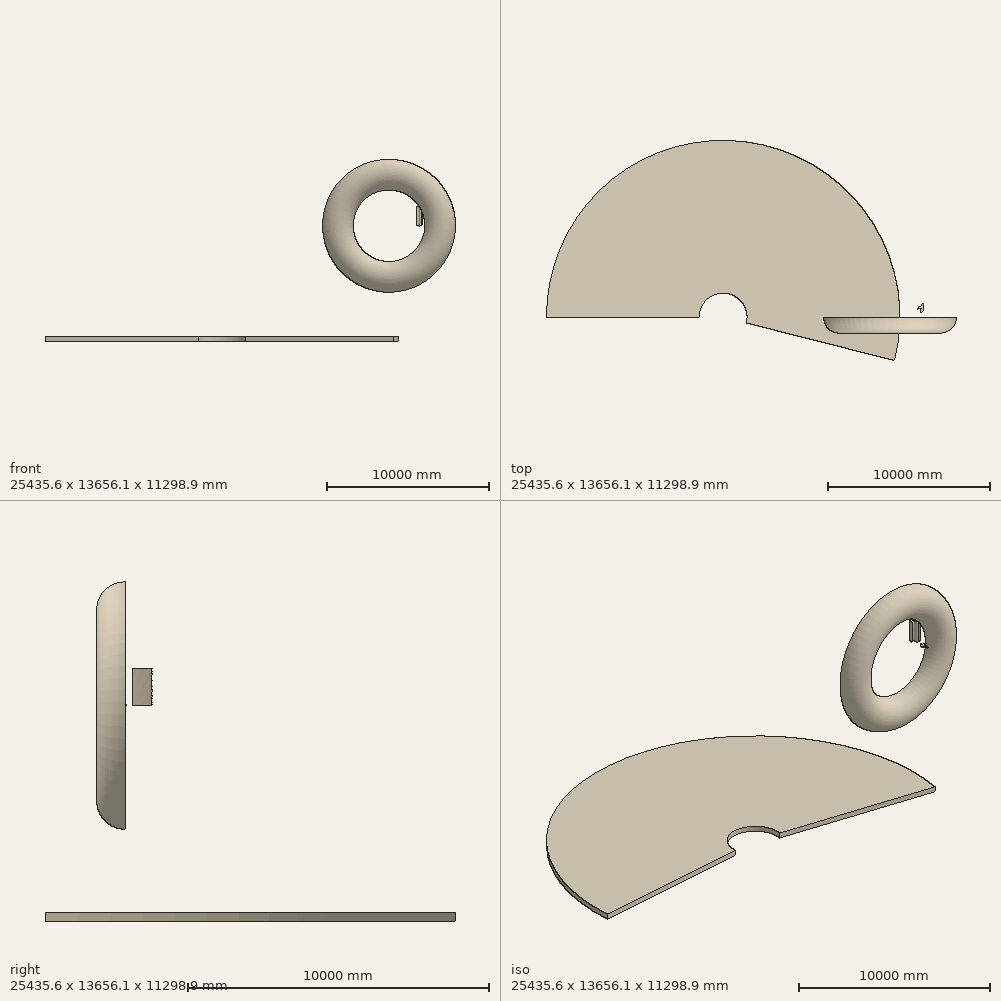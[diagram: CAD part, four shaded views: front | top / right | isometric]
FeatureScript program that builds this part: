
annotation { "Feature Type Name" : "Feature", "Feature Type Description" : "" }
export const myFeature = defineFeature(function(context is Context, id is Id, definition is map)
    precondition{}
    {
        {
            var Q0;
            Q0=qCreatedBy(makeId("Top.planeOp"),FACE);
            var sketch = newSketch(context, id + "F0", { "sketchPlane" : qUnion([Q0])});
            skLineSegment(sketch, "E0.bottom", {"start": v(92.01, -36.07) * mm, "end": v(2632.65, -36.07) * mm});
            skLineSegment(sketch, "E0.top", {"start": v(92.01, 26.16) * mm, "end": v(2632.65, 26.16) * mm});
            skLineSegment(sketch, "E0.left", {"start": v(92.01, -36.07) * mm, "end": v(92.01, 26.16) * mm});
            skLineSegment(sketch, "E0.right", {"start": v(2632.65, -36.07) * mm, "end": v(2632.65, 26.16) * mm});
            skCircle(sketch, "E1", {"center": v(1260.53, -36.07) * mm, "radius": 952.82 * mm});
            skLineSegment(sketch, "E2", {"start": v(3070.5, 365.53) * mm, "end": v(3158.96, -409.32) * mm});
            skLineSegment(sketch, "E3", {"start": v(-1908.37, -1224.54) * mm, "end": v(-1908.37, 739.22) * mm, "construction": true});
            skSolve(sketch);
        }
        {
            var Q0;
            Q0=sQuery(id+"F0.wireOp",EDGE,"E0.top");
            var Q1;
            Q1=sQuery(id+"F0.wireOp",EDGE,"E0.bottom");
            var Q2;
            Q2=sQuery(id+"F0.wireOp",EDGE,"E2");
            revolve(context, id + "F1", {"bodyType" : ToolBodyType.SURFACE, "surfaceEntities" : qUnion([Q0, Q1]), "axis" : qUnion([Q2]), "revolveType" : RevolveType.FULL});
        }
        {
            var Q0;
            {var subQ0=sQuery(id+"F0.wireOp",EDGE,"E1");var subQ1=sQuery(id+"F0.wireOp",EDGE,"E0.bottom");var subQ2=makeQuery(id+"F0.imprint","INTERSECT",VERTEX,{"disambiguationData":[OD(0.0)],"derivedFrom":[subQ1,subQ0]});Q0=makeQuery(id+"F0.imprint","IMPRINT",FACE,{"disambiguationData":[TD([[makeQuery(id+"F0.imprint","IMPRINT",EDGE,{"disambiguationData":[TD([[subQ2,-1.0]])],"derivedFrom":subQ1}),-1.0]])]});}
            var Q1;
            Q1=sQuery(id+"F0.wireOp",EDGE,"E3");
            revolve(context, id + "F12", {"entities" : qUnion([Q0]), "axis" : qUnion([Q1]), "revolveType" : RevolveType.FULL});
        }
        {
            var Q0;
            Q0=qCreatedBy(makeId("Front.planeOp"),FACE);
            var sketch = newSketch(context, id + "F13", { "sketchPlane" : qUnion([Q0])});
            skLineSegment(sketch, "E4.bottom", {"start": v(-13740.44, -6881.52) * mm, "end": v(-23222.2, -6881.52) * mm});
            skLineSegment(sketch, "E4.top", {"start": v(-13740.44, -7177.15) * mm, "end": v(-23222.2, -7177.15) * mm});
            skLineSegment(sketch, "E4.left", {"start": v(-13740.44, -6881.52) * mm, "end": v(-13740.44, -7177.15) * mm});
            skLineSegment(sketch, "E4.right", {"start": v(-23222.2, -6881.52) * mm, "end": v(-23222.2, -7177.15) * mm});
            skLineSegment(sketch, "E5", {"start": v(-12259.04, -6137.5) * mm, "end": v(-12259.04, -8157.46) * mm, "construction": true});
            skSolve(sketch);
        }
        {
            var Q0;
            Q0=makeQuery(id+"F13.imprint","IMPRINT",FACE,{"disambiguationData":[TD([[makeQuery(id+"F13.imprint","IMPRINT",EDGE,{"derivedFrom":sQuery(id+"F13.wireOp",EDGE,"E4.bottom")}),1.0]])]});
            var Q1;
            Q1=sQuery(id+"F13.wireOp",EDGE,"E5");
            revolve(context, id + "F14", {"entities" : qUnion([Q0]), "axis" : qUnion([Q1]), "revolveType" : RevolveType.ONE_DIRECTION, "angle" : 194.22 * degree});
        }
        {
            var Q0;
            Q0=qCreatedBy(makeId("Front.planeOp"),FACE);
            var sketch = newSketch(context, id + "F15", { "sketchPlane" : qUnion([Q0])});
            skCircle(sketch, "E6", {"center": v(0, 0) * mm, "radius": 35.02 * mm});
            skSolve(sketch);
        }
        {
            var Q0;
            Q0 = qSketchRegion(id + "F15", true);
            extrude(context, id + "F16", {"entities" : qUnion([Q0]), "depth" : 23.8 * mm});
        }
        {
            var Q0;
            Q0=makeQuery(id+"F16.opExtrude","CAP_EDGE",EDGE,{"disambiguationData":[OSD([sQuery(id+"F15.wireOp",EDGE,"E6")])],"isStart":false});
            var Q1;
            Q1=makeQuery(id+"F16.opExtrude","CAP_EDGE",EDGE,{"disambiguationData":[OSD([sQuery(id+"F15.wireOp",EDGE,"E6")])],"isStart":true});
            fillet(context, id + "F17", {"entities" : qUnion([Q0, Q1]), "radius" : 3.17 * mm, "tangentPropagation" : true, "allowEdgeOverflow" : false});
        }
        {
            var Q0;
            Q0=qCreatedBy(makeId("Right.planeOp"),FACE);
            var sketch = newSketch(context, id + "F2", { "sketchPlane" : qUnion([Q0])});
            skLineSegment(sketch, "E7", {"start": v(-3.18, -35.02) * mm, "end": v(-20.64, -35.02) * mm});
            skLineSegment(sketch, "E8", {"start": v(-20.64, 35.02) * mm, "end": v(-3.18, 35.02) * mm});
            skCircle(sketch, "E9", {"center": v(-12.03, 2.87) * mm, "radius": 4.97 * mm});
            skLineSegment(sketch, "E10", {"start": v(-70.86, 0) * mm, "end": v(33.05, 0) * mm, "construction": true});
            skSolve(sketch);
        }
        {
            var Q0;
            Q0 = qSketchRegion(id + "F2", true);
            extrude(context, id + "F3", {"entities" : qUnion([Q0]), "operationType" : NewBodyOperationType.REMOVE, "endBound" : BoundingType.UP_TO_NEXT, "oppositeDirection" : true, "depth" : 25.4 * mm});
        }
        {
            var Q0;
            Q0=makeQuery(id+"F16.opExtrude","SWEPT_BODY",BODY,{"disambiguationData":[OSD([sQuery(id+"F15.wireOp",EDGE,"E6")])]});
            var Q1;
            Q1=sQuery(id+"F2.wireOp",EDGE,"E10");
            circularPattern(context, id + "F4", {"entities" : qUnion([Q0]), "axis" : qUnion([Q1]), "angle" : 360 * degree, "instanceCount" : 4, "equalSpace" : true});
        }
        {
            var Q0;
            Q0=qCreatedBy(makeId("Top.planeOp"),FACE);
            var sketch = newSketch(context, id + "F18", { "sketchPlane" : qUnion([Q0])});
            skFitSpline(sketch, "E11", {"points": [v(48.55, -173.31) * mm, v(174.03, -207.84) * mm, v(-172.04, -133.26) * mm, v(-39.91, -410.74) * mm], "startDerivative": vector(973.41, -839.18) * mm, "endDerivative": vector(668.36, 461.78) * mm});
            skFitSpline(sketch, "E12", {"points": [v(-260.6, 355.06) * mm, v(21.41, 497.79) * mm, v(-15.8, 374.19) * mm, v(85.32, 312.25) * mm], "startDerivative": vector(565.05, 1513.97) * mm, "endDerivative": vector(221.65, 1520) * mm});
            skFitSpline(sketch, "E13", {"points": [v(173.83, 382.94) * mm, v(146.98, 851.05) * mm, v(-80.23, 756.18) * mm], "startDerivative": vector(59.43, -2905.2) * mm, "endDerivative": vector(-550.41, 2215.66) * mm});
            skLineSegment(sketch, "E14", {"start": v(-39.91, -410.74) * mm, "end": v(-24.84, -592.9) * mm});
            skLineSegment(sketch, "E15", {"start": v(-24.84, -592.9) * mm, "end": v(48.55, -173.31) * mm});
            skLineSegment(sketch, "E16", {"start": v(85.32, 312.25) * mm, "end": v(173.83, 382.94) * mm});
            skLineSegment(sketch, "E17", {"start": v(-260.6, 355.06) * mm, "end": v(-80.23, 756.18) * mm});
            skSolve(sketch);
        }
        {
            var Q0;
            Q0=makeQuery(id+"F18.imprint","IMPRINT",FACE,{"disambiguationData":[TD([[makeQuery(id+"F18.imprint","IMPRINT",EDGE,{"derivedFrom":sQuery(id+"F18.wireOp",EDGE,"E11")}),1.0]])]});
            extrude(context, id + "F5", {"entities" : qUnion([Q0]), "depth" : ((12 * 3)) * mm});
        }
        {
            var Q0;
            {var subQ4=sQuery(id+"F18.wireOp",EDGE,"E13");Q0=makeQuery(id+"F18.imprint","IMPRINT",FACE,{"disambiguationData":[TD([[makeQuery(id+"F18.imprint","IMPRINT",EDGE,{"derivedFrom":subQ4}),1.0]])]});}
            extrude(context, id + "F6", {"entities" : qUnion([Q0]), "depth" : 1219.2 * mm});
        }
        {
            var Q0;
            Q0=qCreatedBy(makeId("Top.planeOp"),FACE);
            var sketch = newSketch(context, id + "F19", { "sketchPlane" : qUnion([Q0])});
            skLineSegment(sketch, "E18", {"start": v(0, 76) * mm, "end": v(48.41, 0) * mm});
            skLineSegment(sketch, "E19", {"start": v(48.41, 0) * mm, "end": v(-48.41, 0) * mm});
            skLineSegment(sketch, "E20", {"start": v(-48.41, 0) * mm, "end": v(0, 76) * mm});
            skLineSegment(sketch, "E21", {"start": v(-69.43, -15.77) * mm, "end": v(63.9, -15.77) * mm, "construction": true});
            skLineSegment(sketch, "E22.MirrorCS", {"start": v(0, -107.54) * mm, "end": v(48.41, -31.54) * mm});
            skLineSegment(sketch, "E23.MirrorCS", {"start": v(48.41, -31.54) * mm, "end": v(-48.41, -31.54) * mm});
            skLineSegment(sketch, "E24.MirrorCS", {"start": v(-48.41, -31.54) * mm, "end": v(0, -107.54) * mm});
            skSolve(sketch);
        }
        {
            var Q0;
            Q0 = qSketchRegion(id + "F19", true);
            var Q1;
            Q1=sQuery(id+"F19.wireOp",EDGE,"E20");
            var Q2;
            Q2=sQuery(id+"F19.wireOp",EDGE,"E18");
            var Q3;
            Q3=sQuery(id+"F19.wireOp",EDGE,"E19");
            var Q4;
            Q4=sQuery(id+"F19.wireOp",EDGE,"E23.MirrorCS");
            var Q5;
            Q5=sQuery(id+"F19.wireOp",EDGE,"E22.MirrorCS");
            var Q6;
            Q6=sQuery(id+"F19.wireOp",EDGE,"E24.MirrorCS");
            extrude(context, id + "F7", {"entities" : qUnion([Q0]), "bodyType" : ToolBodyType.SURFACE, "surfaceEntities" : qUnion([Q1, Q2, Q3, Q4, Q5, Q6]), "endBound" : BoundingType.SYMMETRIC, "depth" : 152.4 * mm});
        }
        {
            var Q0;
            Q0=qCreatedBy(makeId("Top.planeOp"),FACE);
            var sketch = newSketch(context, id + "F8", { "sketchPlane" : qUnion([Q0])});
            skCircle(sketch, "E25.cCircle", {"center": v(823.84, 0) * mm, "radius": 155.72 * mm, "construction": true});
            skLineSegment(sketch, "E25.0", {"start": v(989.63, -69.6) * mm, "end": v(846.46, -178.38) * mm});
            skLineSegment(sketch, "E25.1", {"start": v(846.46, -178.38) * mm, "end": v(680.66, -108.78) * mm});
            skLineSegment(sketch, "E25.2", {"start": v(680.66, -108.78) * mm, "end": v(658.05, 69.6) * mm});
            skLineSegment(sketch, "E25.3", {"start": v(658.05, 69.6) * mm, "end": v(801.22, 178.38) * mm});
            skLineSegment(sketch, "E25.4", {"start": v(801.22, 178.38) * mm, "end": v(967.02, 108.78) * mm});
            skLineSegment(sketch, "E25.5", {"start": v(967.02, 108.78) * mm, "end": v(989.63, -69.6) * mm});
            skPoint(sketch, "E25.0.midPoint", {"position": v(918.04, -124) * mm});
            skCircle(sketch, "E26.cCircle", {"center": v(814.87, 558.57) * mm, "radius": 188.4 * mm, "construction": true});
            skLineSegment(sketch, "E26.0", {"start": v(1003.28, 695.46) * mm, "end": v(1003.28, 421.69) * mm});
            skLineSegment(sketch, "E26.1", {"start": v(1003.28, 421.69) * mm, "end": v(742.9, 337.09) * mm});
            skLineSegment(sketch, "E26.2", {"start": v(742.9, 337.09) * mm, "end": v(581.98, 558.57) * mm});
            skLineSegment(sketch, "E26.3", {"start": v(581.98, 558.57) * mm, "end": v(742.9, 780.06) * mm});
            skLineSegment(sketch, "E26.4", {"start": v(742.9, 780.06) * mm, "end": v(1003.28, 695.46) * mm});
            skPoint(sketch, "E26.0.midPoint", {"position": v(1003.28, 558.57) * mm});
            skSolve(sketch);
        }
        {
            var Q0;
            Q0 = qSketchRegion(id + "F8", true);
            var Q1;
            Q1 = qBodyType(qCreatedBy(id + "F8" ,EDGE), BodyType.WIRE);
            extrude(context, id + "F9", {"entities" : qUnion([Q0]), "bodyType" : ToolBodyType.SURFACE, "surfaceEntities" : qUnion([Q1]), "endBound" : BoundingType.SYMMETRIC, "depth" : 152.4 * mm});
        }
        {
            var Q0;
            Q0=qCreatedBy(makeId("Top.planeOp"),FACE);
            var sketch = newSketch(context, id + "F10", { "sketchPlane" : qUnion([Q0])});
            skLineSegment(sketch, "E27", {"start": v(0, 0) * mm, "end": v(1159.15, 593.85) * mm});
            skSolve(sketch);
        }
        {
            var Q0;
            Q0 = qSketchRegion(id + "F10", true);
            var Q1;
            Q1=sQuery(id+"F10.wireOp",EDGE,"E27");
            extrude(context, id + "F11", {"entities" : qUnion([Q0]), "bodyType" : ToolBodyType.SURFACE, "surfaceEntities" : qUnion([Q1]), "endBound" : BoundingType.SYMMETRIC, "depth" : 26.99 * mm});
        }
    });
